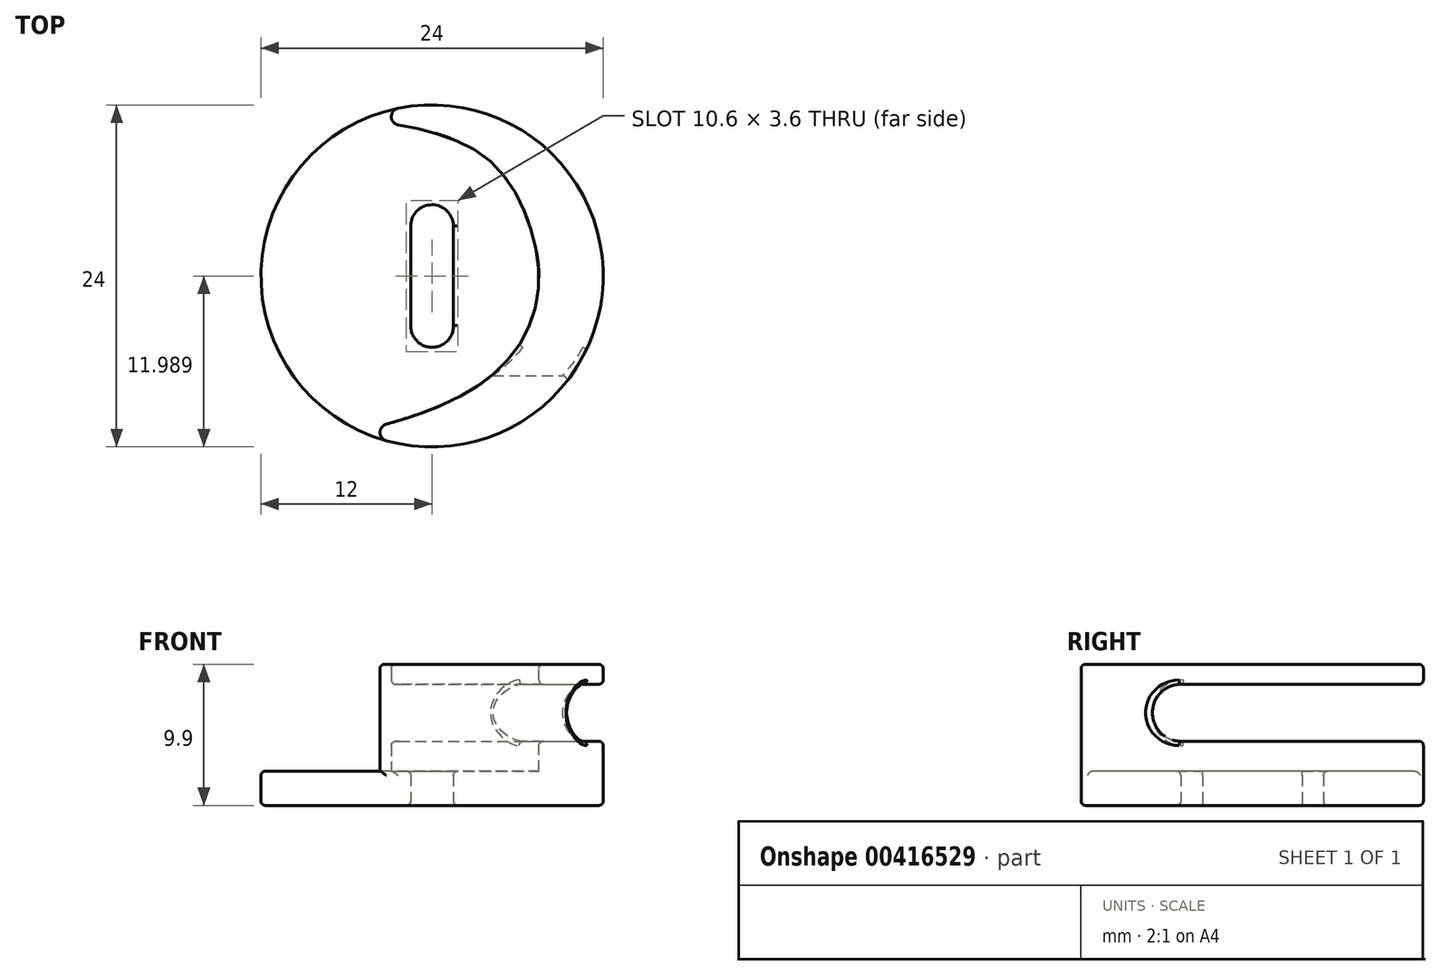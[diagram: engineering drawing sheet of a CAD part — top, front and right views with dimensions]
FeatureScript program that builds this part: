
annotation { "Feature Type Name" : "Feature", "Feature Type Description" : "" }
export const myFeature = defineFeature(function(context is Context, id is Id, definition is map)
    precondition{}
    {
        {
            var Q0;
            Q0=qCreatedBy(makeId("Top.planeOp"),FACE);
            var sketch = newSketch(context, id + "F0", { "sketchPlane" : qUnion([Q0])});
            skCircle(sketch, "E0", {"center": v(0, 0) * mm, "radius": 12 * mm});
            skLineSegment(sketch, "E1.left", {"start": v(1.5, 3.51) * mm, "end": v(1.5, -3.49) * mm});
            skLineSegment(sketch, "E1.right", {"start": v(-1.5, 3.49) * mm, "end": v(-1.5, -3.51) * mm});
            skArc(sketch, "E2", {"start": v(1.5, 3.51) * mm, "mid": v(-0.01, 4.99) * mm, "end": v(-1.5, 3.49) * mm});
            skArc(sketch, "E3", {"start": v(-1.5, -3.51) * mm, "mid": v(0.01, -5.01) * mm, "end": v(1.5, -3.49) * mm});
            skSolve(sketch);
        }
        {
            var Q0;
            Q0 = qSketchRegion(id + "F0", true);
            extrude(context, id + "F1", {"entities" : qUnion([Q0]), "depth" : 2.4 * mm});
        }
        {
            var Q0;
            Q0=makeQuery(id+"F1.opExtrude","CAP_FACE",FACE,{"disambiguationData":[OSD([sQuery(id+"F0.wireOp",EDGE,"E0"),sQuery(id+"F0.wireOp",EDGE,"E1.left"),sQuery(id+"F0.wireOp",EDGE,"E1.right"),sQuery(id+"F0.wireOp",EDGE,"E2"),sQuery(id+"F0.wireOp",EDGE,"E3")])],"isStart":false});
            var sketch = newSketch(context, id + "F2", { "sketchPlane" : qUnion([Q0])});
            skLineSegment(sketch, "E4", {"start": v(-5, -13.7) * mm, "end": v(-5, 17.28) * mm, "construction": true});
            skPoint(sketch, "E5", {"position": v(7.5, 0) * mm});
            skPoint(sketch, "E6", {"position": v(-5, 10.9) * mm});
            skPoint(sketch, "E7", {"position": v(6, -5.01) * mm});
            skPoint(sketch, "E8", {"position": v(-1.5, 10.43) * mm});
            skPoint(sketch, "E8.positionSnap0", {"position": v(-1.5, -0.01) * mm});
            skPoint(sketch, "E9", {"position": v(2.8, 8.96) * mm});
            skPoint(sketch, "E10", {"position": v(5.84, 5.84) * mm});
            skPoint(sketch, "E11", {"position": v(1.7, -8.6) * mm});
            skPoint(sketch, "E12", {"position": v(-5, -10.9) * mm});
            skFitSpline(sketch, "E13", {"points": [v(-5, 10.9) * mm, v(-1.5, 10.43) * mm, v(2.8, 8.96) * mm, v(5.84, 5.84) * mm, v(7.5, 0) * mm, v(6, -5.01) * mm, v(1.7, -8.6) * mm, v(-5, -10.9) * mm], "startDerivative": vector(28.46, -2.94) * mm, "endDerivative": vector(-42.04, -11.63) * mm});
            skSolve(sketch);
        }
        {
            var Q0;
            {var subQ0=sQuery(id+"F2.wireOp",EDGE,"E13");Q0=makeQuery(id+"F2.imprint","IMPRINT",FACE,{"disambiguationData":[TD([[makeQuery(id+"F2.imprint","IMPRINT",EDGE,{"derivedFrom":subQ0}),1.0]])]});}
            extrude(context, id + "F3", {"entities" : qUnion([Q0]), "operationType" : NewBodyOperationType.ADD, "depth" : 7.5 * mm});
        }
        {
            var Q0;
            {var subQ0=sQuery(id+"F2.wireOp",EDGE,"E13");var subQ1=sQuery(id+"F0.wireOp",EDGE,"E0");Q0=makeQuery(id+"F3.opExtrude","SWEPT_EDGE",EDGE,{"disambiguationData":[OSD([subQ1,subQ0]),TDD([makeQuery(id+"F2.imprint","INTERSECT",VERTEX,{"disambiguationData":[OD(1.0)],"derivedFrom":[makeQuery(id+"F1.opExtrude","CAP_EDGE",EDGE,{"disambiguationData":[OSD([subQ1])],"isStart":false}),subQ0]})])]});}
            var Q1;
            {var subQ0=sQuery(id+"F2.wireOp",EDGE,"E13");var subQ1=sQuery(id+"F0.wireOp",EDGE,"E0");Q1=makeQuery(id+"F3.opExtrude","SWEPT_EDGE",EDGE,{"disambiguationData":[OSD([subQ1,subQ0]),TDD([makeQuery(id+"F2.imprint","INTERSECT",VERTEX,{"disambiguationData":[OD(0.0)],"derivedFrom":[makeQuery(id+"F1.opExtrude","CAP_EDGE",EDGE,{"disambiguationData":[OSD([subQ1])],"isStart":false}),subQ0]})])]});}
            fillet(context, id + "F4", {"entities" : qUnion([Q0, Q1]), "radius" : 0.6 * mm, "tangentPropagation" : true, "allowEdgeOverflow" : false});
        }
        {
            var Q0;
            Q0=qCreatedBy(makeId("Right.planeOp"),FACE);
            cPlane(context, id + "F5", {"entities" : qUnion([Q0]), "cplaneType" : CPlaneType.OFFSET, "offset" : 12.5 * mm, "width" : 150 * mm, "height" : 150 * mm});
        }
        {
            var Q0;
            Q0=qCreatedBy(id+"F5.planeOp",FACE);
            var sketch = newSketch(context, id + "F6", { "sketchPlane" : qUnion([Q0])});
            skLineSegment(sketch, "E14.bottom", {"start": v(-5, 8.5) * mm, "end": v(13, 8.5) * mm});
            skLineSegment(sketch, "E14.top", {"start": v(-5, 4.5) * mm, "end": v(13, 4.5) * mm});
            skLineSegment(sketch, "E14.right", {"start": v(13, 8.5) * mm, "end": v(13, 4.5) * mm});
            skArc(sketch, "E15", {"start": v(-5, 8.5) * mm, "mid": v(-7, 6.5) * mm, "end": v(-5, 4.5) * mm});
            skSolve(sketch);
        }
        {
            var Q0;
            Q0=makeQuery(id+"F6.imprint","IMPRINT",FACE,{"disambiguationData":[TD([[makeQuery(id+"F6.imprint","IMPRINT",EDGE,{"derivedFrom":sQuery(id+"F6.wireOp",EDGE,"E14.bottom")}),-1.0]])]});
            extrude(context, id + "F7", {"entities" : qUnion([Q0]), "operationType" : NewBodyOperationType.REMOVE, "oppositeDirection" : true, "depth" : 25 * mm});
        }
        {
            var Q0;
            Q0=makeQuery(id+"F1.opExtrude","CAP_EDGE",EDGE,{"disambiguationData":[OSD([sQuery(id+"F0.wireOp",EDGE,"E0")])],"isStart":true});
            var Q1;
            Q1=makeQuery(id+"F1.opExtrude","CAP_EDGE",EDGE,{"disambiguationData":[OSD([sQuery(id+"F0.wireOp",EDGE,"E0")])],"isStart":false});
            var Q2;
            Q2=makeQuery(id+"F3.opExtrude","CAP_EDGE",EDGE,{"disambiguationData":[OSD([sQuery(id+"F2.wireOp",EDGE,"E13")])],"isStart":true});
            var Q3;
            Q3=makeQuery(id+"F3.opExtrude","CAP_EDGE",EDGE,{"disambiguationData":[OSD([sQuery(id+"F2.wireOp",EDGE,"E13")])],"isStart":false});
            var Q4;
            {var subQ0=sQuery(id+"F2.wireOp",EDGE,"E13");var subQ1=sQuery(id+"F0.wireOp",EDGE,"E0");Q4=makeQuery(id+"F4.opFillet","BLEND_EDGE",EDGE,{"blendedFrom":[makeQuery(id+"F3.opExtrude","SWEPT_EDGE",EDGE,{"disambiguationData":[OSD([subQ1,subQ0]),TDD([makeQuery(id+"F2.imprint","INTERSECT",VERTEX,{"disambiguationData":[OD(1.0)],"derivedFrom":[makeQuery(id+"F1.opExtrude","CAP_EDGE",EDGE,{"disambiguationData":[OSD([subQ1])],"isStart":false}),subQ0]})])]}),makeQuery(id+"F3.opExtrude","CAP_FACE",FACE,{"disambiguationData":[OSD([subQ1,subQ0])],"isStart":false})],"blendedInto":[makeQuery(id+"F3.opExtrude","CAP_FACE",FACE,{"disambiguationData":[OSD([subQ1,subQ0])],"isStart":false})]});}
            var Q5;
            Q5=makeQuery(id+"F3.opExtrude","CAP_EDGE",EDGE,{"disambiguationData":[OSD([sQuery(id+"F0.wireOp",EDGE,"E0")])],"isStart":false});
            var Q6;
            {var subQ0=sQuery(id+"F2.wireOp",EDGE,"E13");var subQ1=sQuery(id+"F0.wireOp",EDGE,"E0");Q6=makeQuery(id+"F4.opFillet","BLEND_EDGE",EDGE,{"blendedFrom":[makeQuery(id+"F3.opExtrude","SWEPT_EDGE",EDGE,{"disambiguationData":[OSD([subQ1,subQ0]),TDD([makeQuery(id+"F2.imprint","INTERSECT",VERTEX,{"disambiguationData":[OD(0.0)],"derivedFrom":[makeQuery(id+"F1.opExtrude","CAP_EDGE",EDGE,{"disambiguationData":[OSD([subQ1])],"isStart":false}),subQ0]})])]}),makeQuery(id+"F3.opExtrude","CAP_FACE",FACE,{"disambiguationData":[OSD([subQ1,subQ0])],"isStart":false})],"blendedInto":[makeQuery(id+"F3.opExtrude","CAP_FACE",FACE,{"disambiguationData":[OSD([subQ1,subQ0])],"isStart":false})]});}
            var Q7;
            {var subQ0=sQuery(id+"F0.wireOp",EDGE,"E0");Q7=makeQuery(id+"F7.boolean.opBoolean","INTERSECT",EDGE,{"derivedFrom":[makeQuery(id+"F3.boolean.opBoolean","MERGE",FACE,{"derivedFrom":[makeQuery(id+"F1.opExtrude","SWEPT_FACE",FACE,{"disambiguationData":[OSD([subQ0])]}),makeQuery(id+"F3.opExtrude","SWEPT_FACE",FACE,{"disambiguationData":[OSD([subQ0])]})]}),makeQuery(id+"F7.opExtrude","SWEPT_FACE",FACE,{"disambiguationData":[OSD([sQuery(id+"F6.wireOp",EDGE,"E14.top")])]})]});}
            var Q8;
            {var subQ0=sQuery(id+"F2.wireOp",EDGE,"E13");var subQ1=sQuery(id+"F0.wireOp",EDGE,"E0");Q8=makeQuery(id+"F7.boolean.opBoolean","INTERSECT",EDGE,{"derivedFrom":[makeQuery(id+"F4.opFillet","BLEND_FACE",FACE,{"disambiguationData":[OSD([subQ1,subQ0]),TDD([makeQuery(id+"F3.opExtrude","SWEPT_EDGE",EDGE,{"disambiguationData":[OSD([subQ1,subQ0]),TDD([makeQuery(id+"F2.imprint","INTERSECT",VERTEX,{"disambiguationData":[OD(0.0)],"derivedFrom":[makeQuery(id+"F1.opExtrude","CAP_EDGE",EDGE,{"disambiguationData":[OSD([subQ1])],"isStart":false}),subQ0]})])]})])]}),makeQuery(id+"F7.opExtrude","SWEPT_FACE",FACE,{"disambiguationData":[OSD([sQuery(id+"F6.wireOp",EDGE,"E14.top")])]})]});}
            var Q9;
            Q9=makeQuery(id+"F7.boolean.opBoolean","INTERSECT",EDGE,{"derivedFrom":[makeQuery(id+"F3.opExtrude","SWEPT_FACE",FACE,{"disambiguationData":[OSD([sQuery(id+"F2.wireOp",EDGE,"E13")])]}),makeQuery(id+"F7.opExtrude","SWEPT_FACE",FACE,{"disambiguationData":[OSD([sQuery(id+"F6.wireOp",EDGE,"E14.top")])]})]});
            var Q10;
            Q10=makeQuery(id+"F7.boolean.opBoolean","INTERSECT",EDGE,{"derivedFrom":[makeQuery(id+"F3.opExtrude","SWEPT_FACE",FACE,{"disambiguationData":[OSD([sQuery(id+"F2.wireOp",EDGE,"E13")])]}),makeQuery(id+"F7.opExtrude","SWEPT_FACE",FACE,{"disambiguationData":[OSD([sQuery(id+"F6.wireOp",EDGE,"E15")])]})]});
            var Q11;
            Q11=makeQuery(id+"F7.boolean.opBoolean","INTERSECT",EDGE,{"derivedFrom":[makeQuery(id+"F3.opExtrude","SWEPT_FACE",FACE,{"disambiguationData":[OSD([sQuery(id+"F2.wireOp",EDGE,"E13")])]}),makeQuery(id+"F7.opExtrude","SWEPT_FACE",FACE,{"disambiguationData":[OSD([sQuery(id+"F6.wireOp",EDGE,"E14.bottom")])]})]});
            var Q12;
            Q12=makeQuery(id+"F1.opExtrude","CAP_EDGE",EDGE,{"disambiguationData":[OSD([sQuery(id+"F0.wireOp",EDGE,"E1.left")])],"isStart":false});
            var Q13;
            Q13=makeQuery(id+"F1.opExtrude","CAP_EDGE",EDGE,{"disambiguationData":[OSD([sQuery(id+"F0.wireOp",EDGE,"E3")])],"isStart":false});
            var Q14;
            Q14=makeQuery(id+"F1.opExtrude","CAP_EDGE",EDGE,{"disambiguationData":[OSD([sQuery(id+"F0.wireOp",EDGE,"E1.right")])],"isStart":false});
            var Q15;
            Q15=makeQuery(id+"F1.opExtrude","CAP_EDGE",EDGE,{"disambiguationData":[OSD([sQuery(id+"F0.wireOp",EDGE,"E2")])],"isStart":false});
            var Q16;
            Q16=makeQuery(id+"F1.opExtrude","CAP_EDGE",EDGE,{"disambiguationData":[OSD([sQuery(id+"F0.wireOp",EDGE,"E2")])],"isStart":true});
            var Q17;
            Q17=makeQuery(id+"F1.opExtrude","CAP_EDGE",EDGE,{"disambiguationData":[OSD([sQuery(id+"F0.wireOp",EDGE,"E1.right")])],"isStart":true});
            var Q18;
            Q18=makeQuery(id+"F1.opExtrude","CAP_EDGE",EDGE,{"disambiguationData":[OSD([sQuery(id+"F0.wireOp",EDGE,"E3")])],"isStart":true});
            var Q19;
            Q19=makeQuery(id+"F1.opExtrude","CAP_EDGE",EDGE,{"disambiguationData":[OSD([sQuery(id+"F0.wireOp",EDGE,"E1.left")])],"isStart":true});
            fillet(context, id + "F8", {"entities" : qUnion([Q0, Q1, Q2, Q3, Q4, Q5, Q6, Q7, Q8, Q9, Q10, Q11, Q12, Q13, Q14, Q15, Q16, Q17, Q18, Q19]), "radius" : 0.3 * mm, "tangentPropagation" : true, "allowEdgeOverflow" : false});
        }
        {
            var Q0;
            Q0=qCreatedBy(id+"F5.planeOp",FACE);
            var sketch = newSketch(context, id + "F9", { "sketchPlane" : qUnion([Q0])});
            skLineSegment(sketch, "E16", {"start": v(-9.8, 6.5) * mm, "end": v(14.72, 6.5) * mm, "construction": true});
            skPoint(sketch, "E17", {"position": v(0, 6.5) * mm});
            skSolve(sketch);
        }
    });
